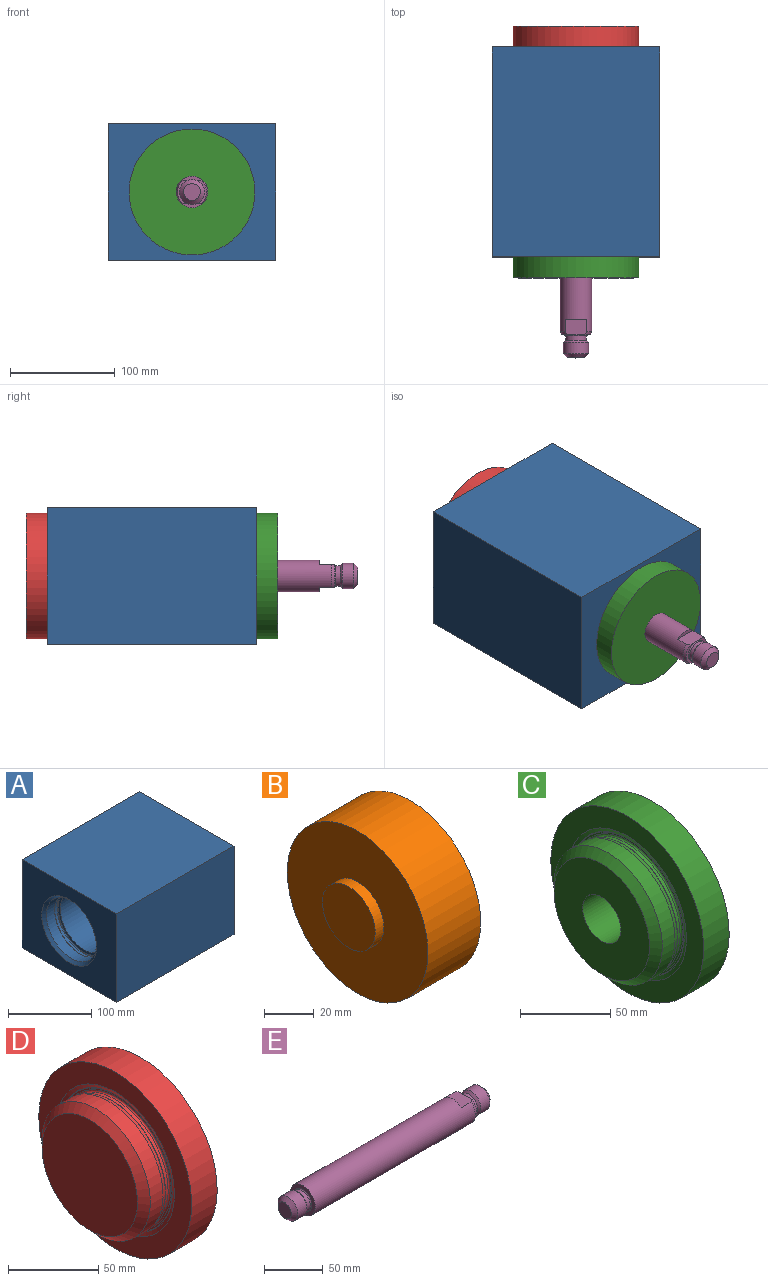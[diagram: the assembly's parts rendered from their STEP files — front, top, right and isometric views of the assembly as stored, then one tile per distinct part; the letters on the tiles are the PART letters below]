
ASSEMBLY  parts=5 mates=4
PART A: 19 faces, bbox 200x160x130 mm
  f0: cylinder r=40mm len=150mm, axis (-1,0,0), area 37699.1mm2, adj f6,f12
  f1: plane 160x130mm, normal (-1,0,0), area 14007.1mm2, adj f5,f15,f16,f17,f18
  f2: plane 160x130mm, normal (1,0,0), area 14007.1mm2, adj f11,f15,f16,f17,f18
  f3: cone r=42.5mm half-angle=45deg, axis (1,0,0), area 773.1mm2, adj f4,f8
  f4: cylinder r=42.5mm len=85mm, axis (1,0,0), area 3738.5mm2, adj f3,f5
  f5: cone r=42.5mm half-angle=45deg, axis (-1,0,0), area 1581.7mm2, adj f1,f4
  f6: plane 87x87mm, normal (-1,0,0), area 918.1mm2, adj f0,f7
  f7: torus R=43.5mm, axis (1,0,0), area 435.6mm2, adj f6,f8
  f8: cylinder r=44.5mm len=89mm, axis (1,0,0), area 1118.4mm2, adj f3,f7
  f9: cone r=42.5mm half-angle=45deg, axis (-1,0,0), area 773.1mm2, adj f10,f14
  f10: cylinder r=42.5mm len=85mm, axis (-1,0,0), area 3738.5mm2, adj f9,f11
  f11: cone r=42.5mm half-angle=45deg, axis (1,0,0), area 1581.7mm2, adj f2,f10
  f12: plane 87x87mm, normal (1,0,0), area 918.1mm2, adj f0,f13
  f13: torus R=43.5mm, axis (-1,0,0), area 435.6mm2, adj f12,f14
  f14: cylinder r=44.5mm len=89mm, axis (-1,0,0), area 1118.4mm2, adj f9,f13
  f15: plane 200x130mm, normal (0,1,0), area 26000mm2, adj f1,f2,f16,f18
  f16: plane 200x160mm, normal (0,0,1), area 32000mm2, adj f1,f2,f15,f17
  f17: plane 200x130mm, normal (0,-1,0), area 26000mm2, adj f1,f2,f16,f18
  f18: plane 200x160mm, normal (0,0,-1), area 32000mm2, adj f1,f2,f15,f17
PART B: 9 faces, bbox 40x80x80 mm
  f0: plane 30x30mm, normal (1,0,0), area 326.7mm2, adj f1,f8
  f1: cylinder r=15mm len=30mm, axis (-1,0,0), area 471.2mm2, adj f0,f2
  f2: plane 80x80mm, normal (1,0,0), area 4319.7mm2, adj f1,f3
  f3: cylinder r=40mm len=80mm, axis (-1,0,0), area 7539.8mm2, adj f2,f4
  f4: plane 80x80mm, normal (-1,0,0), area 4319.7mm2, adj f3,f5
  f5: cylinder r=15mm len=30mm, axis (-1,0,0), area 471.2mm2, adj f4,f6
  f6: plane 30x30mm, normal (-1,0,0), area 706.9mm2, adj f5
  f7: cone r=0mm half-angle=59deg, axis (1,0,0), area 443.5mm2, adj f8
  f8: cylinder r=11mm len=26mm, axis (1,0,0), area 1797mm2, adj f0,f7
PART C: 14 faces, bbox 40x120x120 mm
  f0: cone r=42.5mm half-angle=45deg, axis (1,0,0), area 1777.2mm2, adj f1,f12
  f1: plane 75x75mm, normal (-1,0,0), area 3711mm2, adj f0,f13
  f2: plane 120x120mm, normal (1,0,0), area 10602.9mm2, adj f3,f13
  f3: cylinder r=60mm len=120mm, axis (-1,0,0), area 7539.8mm2, adj f2,f4
  f4: plane 120x120mm, normal (-1,0,0), area 4516.8mm2, adj f3,f5
  f5: cone r=46.5mm half-angle=70deg, axis (-1,0,0), area 780.4mm2, adj f4,f6
  f6: torus R=43.58mm, axis (-1,0,0), area 96mm2, adj f5,f7
  f7: plane 87.15x87.15mm, normal (-1,0,0), area 291mm2, adj f6,f8
  f8: torus R=42.5mm, axis (-1,0,0), area 413.2mm2, adj f7,f9
  f9: cylinder r=41.5mm len=83mm, axis (-1,0,0), area 541.4mm2, adj f8,f10
  f10: torus R=42.5mm, axis (-1,0,0), area 91.1mm2, adj f9,f11
  f11: cone r=41.56mm half-angle=20deg, axis (-1,0,0), area 725.6mm2, adj f10,f12
  f12: cylinder r=42.5mm len=85mm, axis (-1,0,0), area 2670.4mm2, adj f0,f11
  f13: cylinder r=15mm len=40mm, axis (1,0,0), area 3769.9mm2, adj f1,f2
PART D: 13 faces, bbox 40x120x120 mm
  f0: cone r=42.5mm half-angle=45deg, axis (1,0,0), area 1777.2mm2, adj f1,f12
  f1: plane 75x75mm, normal (-1,0,0), area 4417.9mm2, adj f0
  f2: plane 120x120mm, normal (1,0,0), area 11309.7mm2, adj f3
  f3: cylinder r=60mm len=120mm, axis (-1,0,0), area 7539.8mm2, adj f2,f4
  f4: plane 120x120mm, normal (-1,0,0), area 4516.8mm2, adj f3,f5
  f5: cone r=46.5mm half-angle=70deg, axis (-1,0,0), area 780.4mm2, adj f4,f6
  f6: torus R=43.58mm, axis (-1,0,0), area 96mm2, adj f5,f7
  f7: plane 87.15x87.15mm, normal (-1,0,0), area 291mm2, adj f6,f8
  f8: torus R=42.5mm, axis (-1,0,0), area 413.2mm2, adj f7,f9
  f9: cylinder r=41.5mm len=83mm, axis (-1,0,0), area 541.4mm2, adj f8,f10
  f10: torus R=42.5mm, axis (-1,0,0), area 91.1mm2, adj f9,f11
  f11: cone r=41.56mm half-angle=20deg, axis (-1,0,0), area 725.6mm2, adj f10,f12
  f12: cylinder r=42.5mm len=85mm, axis (-1,0,0), area 2670.4mm2, adj f0,f11
PART E: 22 faces, bbox 240.1x30.1x30.1 mm
  f0: cylinder r=15mm len=193mm, axis (1,0,0), area 17651.6mm2, adj f3,f4,f5,f18,f19,f20,f21
  f1: plane 22x13.91mm, normal (1,0,0), area 80mm2, adj f3,f16,f19,f21
  f2: plane 22x13.91mm, normal (1,0,0), area 80mm2, adj f4,f16,f19,f21
  f3: cone r=13.91mm half-angle=20deg, axis (-1,0,0), area 80mm2, adj f0,f1,f19,f21
  f4: cone r=13.91mm half-angle=20deg, axis (-1,0,0), area 80mm2, adj f0,f2,f19,f21
  f5: plane 30x30mm, normal (-1,0,0), area 326.7mm2, adj f0,f10
  f6: cone r=8mm half-angle=45deg, axis (1,0,0), area 355.4mm2, adj f7,f11
  f7: cylinder r=12mm len=24mm, axis (1,0,0), area 829.4mm2, adj f6,f8
  f8: cone r=12mm half-angle=45deg, axis (-1,0,0), area 195.5mm2, adj f7,f9
  f9: cylinder r=10mm len=20mm, axis (1,0,0), area 251.3mm2, adj f8,f10
  f10: torus R=11mm, axis (1,0,0), area 102.3mm2, adj f5,f9
  f11: plane 16x16mm, normal (-1,0,0), area 201.1mm2, adj f6
  f12: cone r=8mm half-angle=45deg, axis (-1,0,0), area 355.4mm2, adj f13,f17
  f13: cylinder r=12mm len=24mm, axis (-1,0,0), area 829.4mm2, adj f12,f14
  f14: cone r=12mm half-angle=45deg, axis (1,0,0), area 195.5mm2, adj f13,f15
  f15: cylinder r=10mm len=20mm, axis (-1,0,0), area 251.3mm2, adj f14,f16
  f16: torus R=11mm, axis (-1,0,0), area 102.3mm2, adj f1,f2,f15
  f17: plane 16x16mm, normal (1,0,0), area 201.1mm2, adj f12
  f18: plane 20.4x4mm, normal (1,0,0), area 56mm2, adj f0,f19
  f19: plane 20.48x15.08mm, normal (0,0,-1), area 301mm2, adj f0,f1,f2,f3,f4,f18
  f20: plane 20.4x4mm, normal (1,0,0), area 56mm2, adj f0,f21
  f21: plane 20.48x15.08mm, normal (0,0,1), area 301mm2, adj f0,f1,f2,f3,f4,f20
PLACE A rot(axis=(0,0,-1),90deg) t=(0,100,0)mm
PLACE B rot(axis=(0,0,-1),90deg) t=(0,21.74,0)mm
PLACE C rot(axis=(0,0,-1),90deg) t=(0,-120,0)mm
PLACE D rot(axis=(0.58,0.58,0.58),120deg) t=(0,120,0)mm
PLACE E rot(axis=(0,0,-1),90deg) t=(0,43.74,0)mm
MATE fastened D.f0 <-> A.f0  axis (0,-1,0) through (0,100,0)mm
MATE fastened C.f0 <-> A.f0  axis (0,1,0) through (0,-100,0)mm
MATE slider B.f1 <-> D.f0  axis (0,1,0) through (0,61.74,0)mm
MATE fastened E.f0 <-> B.f1  axis (0,1,0) through (0,21.74,0)mm
